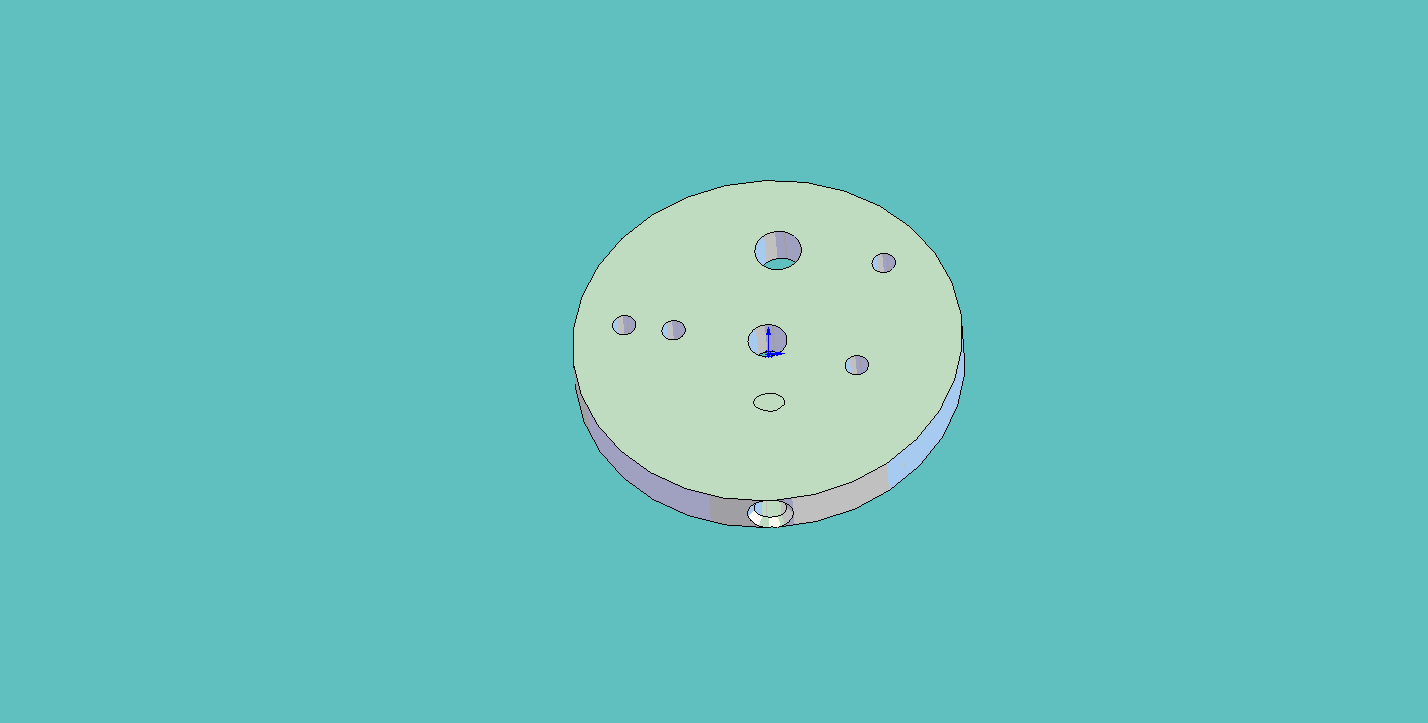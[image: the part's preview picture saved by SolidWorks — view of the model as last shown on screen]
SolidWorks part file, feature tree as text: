
SOLIDWORKS PART (.sldprt)
format: sldprt  version: not decoded by parser v0  size: 179,712 bytes
history: native  units: mm
features: sketch x4, plane x3, material x1, extrude x1, cut_revolve x1, hole x1, thread x1 (+12 scaffold rows collapsed)
feature tree (24):
  scaffold x12  (default folders/planes/origin — collapsed)
  material  "Matériau <non spécifié>"
  plane  "Plan de face"
  plane  "Plan de dessus"
  plane  "Plan de droite"
  sketch  "Esquisse1"  dims[c1.D1=3.0mm c1.D2=5.0mm c1.D3=5.98mm c1.D4=50.0mm c1.D5=3.0mm c1.D6=3.0mm c1.D7=3.0mm c1.D8=3.0mm c1.D9=3.0mm c1.D10=5.98mm c1.D12=3.0mm c1.D13=3.0mm c1.D14=3.0mm c1.D15=3.0mm c2.D5=2.2mm c2.D6=12.0mm c2.D8=18.3mm c2.D9=3.3mm c2.D10=14.0mm c2.D11=1.5mm c2.D12=11.4mm c2.D13=15.0mm c2.D14=11.4mm c2.D15=4.4mm]
  extrude  "Extrusion1"  Depth=6mm
  sketch  "Esquisse2"  dims[c1.D1=4.2mm c1.D2=17.5mm c1.D3=1.0mm c1.D4=~0.678497mm c2.D3=~3.680262mm c3.D3=45.0deg c3.D4=1.0mm]
  cut_revolve  "Enlèvement de matière-Révolution1"  Angle=360deg
  hole  "Trou taraudé M4x0.71"  Diameter=3.3mm Depth=7.5mm
  sketch  "Esquisse3D1"
  sketch  "Esquisse3"  dims[hole-wizard template sketch: 47 standard entries collapsed; hole parameters kept: c15.Profondeur du trou pour taraudage=7.5mm c15.D3=~14.816244mm c15.Angle de pointe=118.0deg]
  thread  "Filetage de perçage1"  Diameter=5.621836mm  [1 undecoded]
decode coverage: 7 of 8 modeling features carry decoded parameters
note: ~ marks probable driven/reference dimensions
note: 1 parameter value undecoded
note: suppression state not decoded; provenance and decode notes live in map.json
